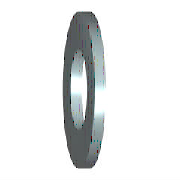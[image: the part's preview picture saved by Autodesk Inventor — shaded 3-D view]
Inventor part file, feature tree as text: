
AUTODESK INVENTOR PART (.ipt)
format: ipt  version: 2020 (Build 240168000, 168)  size: 105,984 bytes
history: native  units: mm (DEFAULTED — no unit token found)
features: extrude x1, other x1, plane x1, sketch x1
ambient origin geometry x7: Origin, YZ Plane, XY Plane, X Axis, Y Axis, Z Axis, Center Point
bodies: Solid1 (feature_tree)
feature tree (4):
  extrude  "Bryła"  Depth=3.2mm
  other  "Work Axis1"
  plane  "Work Plane1"
  sketch  "Szkic"
